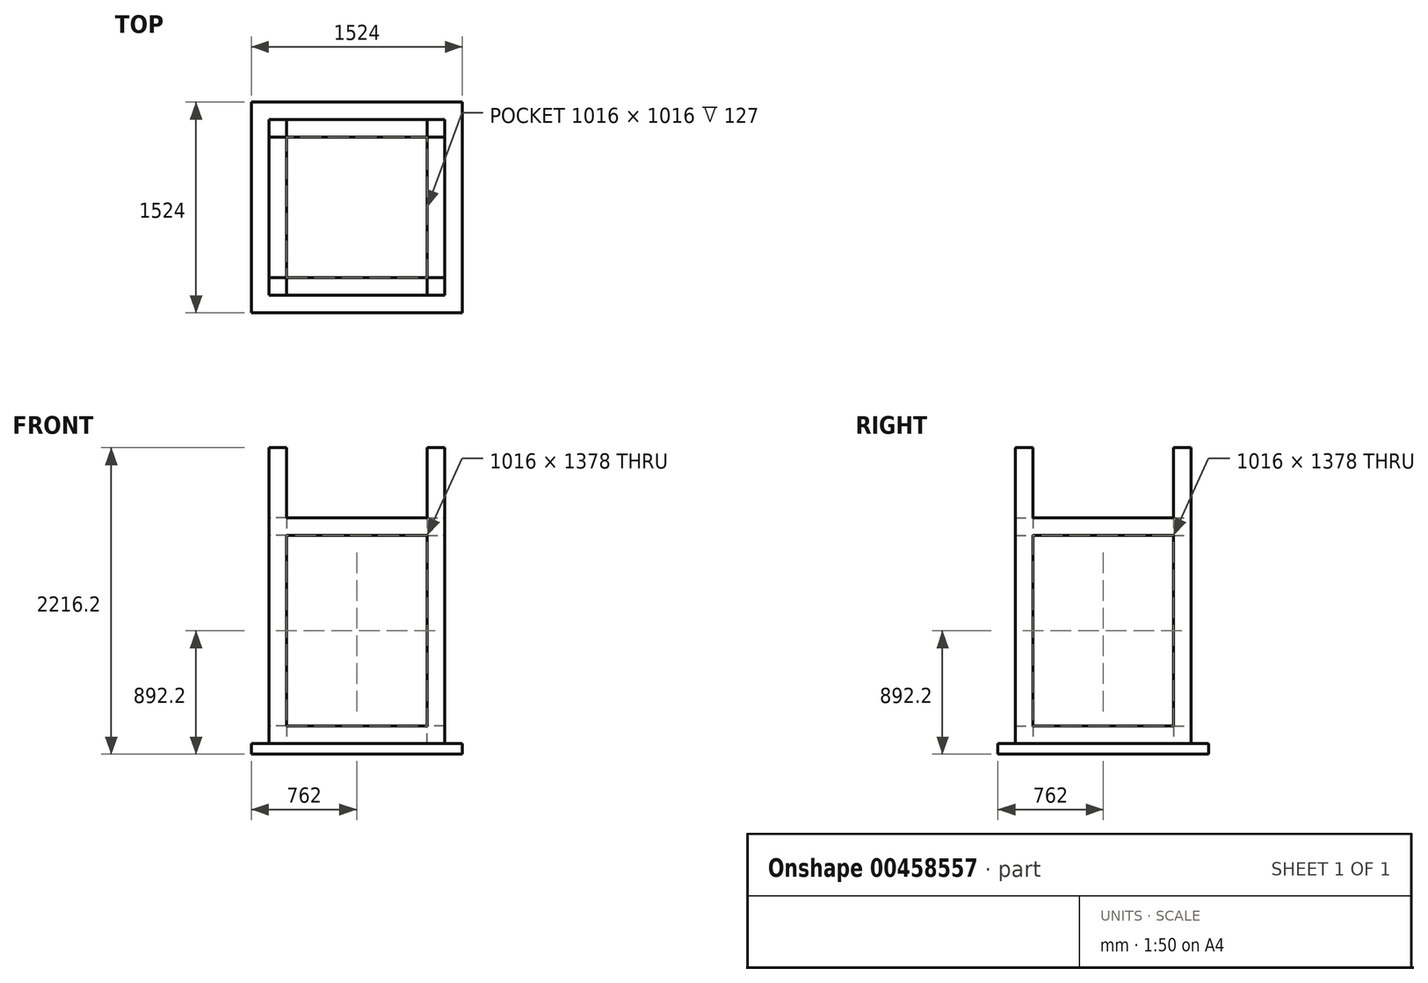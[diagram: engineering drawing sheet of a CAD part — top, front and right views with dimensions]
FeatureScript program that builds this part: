
annotation { "Feature Type Name" : "Feature", "Feature Type Description" : "" }
export const myFeature = defineFeature(function(context is Context, id is Id, definition is map)
    precondition{}
    {
        {
            var Q0;
            Q0=qCreatedBy(makeId("Top.planeOp"),FACE);
            var sketch = newSketch(context, id + "F0", { "sketchPlane" : qUnion([Q0])});
            skLineSegment(sketch, "E0.bottom", {"start": v(0, 1524) * mm, "end": v(1524, 1524) * mm});
            skLineSegment(sketch, "E0.top", {"start": v(0, 0) * mm, "end": v(1524, 0) * mm});
            skLineSegment(sketch, "E0.left", {"start": v(0, 1524) * mm, "end": v(0, 0) * mm});
            skLineSegment(sketch, "E0.right", {"start": v(1524, 1524) * mm, "end": v(1524, 0) * mm});
            skLineSegment(sketch, "E1.bottom", {"start": v(127, 1397) * mm, "end": v(254, 1397) * mm});
            skLineSegment(sketch, "E1.top", {"start": v(127, 1270) * mm, "end": v(254, 1270) * mm});
            skLineSegment(sketch, "E1.left", {"start": v(127, 1397) * mm, "end": v(127, 1270) * mm});
            skLineSegment(sketch, "E1.right", {"start": v(254, 1397) * mm, "end": v(254, 1270) * mm});
            skLineSegment(sketch, "E2.bottom", {"start": v(1270, 1397) * mm, "end": v(1397, 1397) * mm});
            skLineSegment(sketch, "E2.top", {"start": v(1270, 1270) * mm, "end": v(1397, 1270) * mm});
            skLineSegment(sketch, "E2.left", {"start": v(1270, 1397) * mm, "end": v(1270, 1270) * mm});
            skLineSegment(sketch, "E2.right", {"start": v(1397, 1397) * mm, "end": v(1397, 1270) * mm});
            skLineSegment(sketch, "E3.bottom", {"start": v(1270, 254) * mm, "end": v(1397, 254) * mm});
            skLineSegment(sketch, "E3.top", {"start": v(1270, 127) * mm, "end": v(1397, 127) * mm});
            skLineSegment(sketch, "E3.left", {"start": v(1270, 254) * mm, "end": v(1270, 127) * mm});
            skLineSegment(sketch, "E3.right", {"start": v(1397, 254) * mm, "end": v(1397, 127) * mm});
            skLineSegment(sketch, "E4.bottom", {"start": v(127, 254) * mm, "end": v(254, 254) * mm});
            skLineSegment(sketch, "E4.top", {"start": v(127, 127) * mm, "end": v(254, 127) * mm});
            skLineSegment(sketch, "E4.left", {"start": v(127, 254) * mm, "end": v(127, 127) * mm});
            skLineSegment(sketch, "E4.right", {"start": v(254, 254) * mm, "end": v(254, 127) * mm});
            skSolve(sketch);
        }
        {
            var Q0;
            Q0=makeQuery(id+"F0.imprint","IMPRINT",FACE,{"disambiguationData":[TD([[makeQuery(id+"F0.imprint","IMPRINT",EDGE,{"derivedFrom":sQuery(id+"F0.wireOp",EDGE,"E1.bottom")}),-1.0]])]});
            var Q1;
            Q1=makeQuery(id+"F0.imprint","IMPRINT",FACE,{"disambiguationData":[TD([[makeQuery(id+"F0.imprint","IMPRINT",EDGE,{"derivedFrom":sQuery(id+"F0.wireOp",EDGE,"E2.bottom")}),-1.0]])]});
            var Q2;
            Q2=makeQuery(id+"F0.imprint","IMPRINT",FACE,{"disambiguationData":[TD([[makeQuery(id+"F0.imprint","IMPRINT",EDGE,{"derivedFrom":sQuery(id+"F0.wireOp",EDGE,"E3.bottom")}),-1.0]])]});
            var Q3;
            Q3=makeQuery(id+"F0.imprint","IMPRINT",FACE,{"disambiguationData":[TD([[makeQuery(id+"F0.imprint","IMPRINT",EDGE,{"derivedFrom":sQuery(id+"F0.wireOp",EDGE,"E4.bottom")}),-1.0]])]});
            extrude(context, id + "F1", {"entities" : qUnion([Q0, Q1, Q2, Q3]), "depth" : 2140 * mm});
        }
        {
            var Q0;
            Q0=makeQuery(id+"F0.imprint","IMPRINT",FACE,{"disambiguationData":[TD([[makeQuery(id+"F0.imprint","IMPRINT",EDGE,{"derivedFrom":sQuery(id+"F0.wireOp",EDGE,"E0.bottom")}),-1.0]])]});
            var Q1;
            Q1=makeQuery(id+"F0.imprint","IMPRINT",FACE,{"disambiguationData":[TD([[makeQuery(id+"F0.imprint","IMPRINT",EDGE,{"derivedFrom":sQuery(id+"F0.wireOp",EDGE,"E1.bottom")}),-1.0]])]});
            var Q2;
            Q2=makeQuery(id+"F0.imprint","IMPRINT",FACE,{"disambiguationData":[TD([[makeQuery(id+"F0.imprint","IMPRINT",EDGE,{"derivedFrom":sQuery(id+"F0.wireOp",EDGE,"E2.bottom")}),-1.0]])]});
            var Q3;
            Q3=makeQuery(id+"F0.imprint","IMPRINT",FACE,{"disambiguationData":[TD([[makeQuery(id+"F0.imprint","IMPRINT",EDGE,{"derivedFrom":sQuery(id+"F0.wireOp",EDGE,"E3.bottom")}),-1.0]])]});
            var Q4;
            Q4=makeQuery(id+"F0.imprint","IMPRINT",FACE,{"disambiguationData":[TD([[makeQuery(id+"F0.imprint","IMPRINT",EDGE,{"derivedFrom":sQuery(id+"F0.wireOp",EDGE,"E4.bottom")}),-1.0]])]});
            extrude(context, id + "F2", {"entities" : qUnion([Q0, Q1, Q2, Q3, Q4]), "operationType" : NewBodyOperationType.ADD, "oppositeDirection" : true, "depth" : 76.2 * mm});
        }
        {
            var Q0;
            Q0=makeQuery(id+"F1.opExtrude","SWEPT_FACE",FACE,{"disambiguationData":[OSD([sQuery(id+"F0.wireOp",EDGE,"E3.left")])]});
            var sketch = newSketch(context, id + "F3", { "sketchPlane" : qUnion([Q0])});
            skLineSegment(sketch, "E5.bottom", {"start": v(-127, 1505) * mm, "end": v(-254, 1505) * mm});
            skLineSegment(sketch, "E5.top", {"start": v(-127, 1632) * mm, "end": v(-254, 1632) * mm});
            skLineSegment(sketch, "E5.left", {"start": v(-127, 1505) * mm, "end": v(-127, 1632) * mm});
            skLineSegment(sketch, "E5.right", {"start": v(-254, 1505) * mm, "end": v(-254, 1632) * mm});
            skSolve(sketch);
        }
        {
            var Q0;
            Q0=makeQuery(id+"F1.opExtrude","SWEPT_FACE",FACE,{"disambiguationData":[OSD([sQuery(id+"F0.wireOp",EDGE,"E2.top")])]});
            var sketch = newSketch(context, id + "F4", { "sketchPlane" : qUnion([Q0])});
            skLineSegment(sketch, "E6.bottom", {"start": v(1270, 1632) * mm, "end": v(1397, 1632) * mm});
            skLineSegment(sketch, "E6.top", {"start": v(1270, 1505) * mm, "end": v(1397, 1505) * mm});
            skLineSegment(sketch, "E6.left", {"start": v(1270, 1632) * mm, "end": v(1270, 1505) * mm});
            skLineSegment(sketch, "E6.right", {"start": v(1397, 1632) * mm, "end": v(1397, 1505) * mm});
            skSolve(sketch);
        }
        {
            var Q0;
            Q0=makeQuery(id+"F1.opExtrude","SWEPT_FACE",FACE,{"disambiguationData":[OSD([sQuery(id+"F0.wireOp",EDGE,"E1.right")])]});
            var sketch = newSketch(context, id + "F5", { "sketchPlane" : qUnion([Q0])});
            skLineSegment(sketch, "E7.bottom", {"start": v(1397, 1632) * mm, "end": v(1270, 1632) * mm});
            skLineSegment(sketch, "E7.top", {"start": v(1397, 1505) * mm, "end": v(1270, 1505) * mm});
            skLineSegment(sketch, "E7.left", {"start": v(1397, 1632) * mm, "end": v(1397, 1505) * mm});
            skLineSegment(sketch, "E7.right", {"start": v(1270, 1632) * mm, "end": v(1270, 1505) * mm});
            skSolve(sketch);
        }
        {
            var Q0;
            Q0=makeQuery(id+"F1.opExtrude","SWEPT_FACE",FACE,{"disambiguationData":[OSD([sQuery(id+"F0.wireOp",EDGE,"E4.bottom")])]});
            var sketch = newSketch(context, id + "F6", { "sketchPlane" : qUnion([Q0])});
            skLineSegment(sketch, "E8.bottom", {"start": v(-127, 1632) * mm, "end": v(-254, 1632) * mm});
            skLineSegment(sketch, "E8.top", {"start": v(-127, 1505) * mm, "end": v(-254, 1505) * mm});
            skLineSegment(sketch, "E8.left", {"start": v(-127, 1632) * mm, "end": v(-127, 1505) * mm});
            skLineSegment(sketch, "E8.right", {"start": v(-254, 1632) * mm, "end": v(-254, 1505) * mm});
            skSolve(sketch);
        }
        {
            var Q0;
            Q0 = qSketchRegion(id + "F6", true);
            extrude(context, id + "F7", {"entities" : qUnion([Q0]), "operationType" : NewBodyOperationType.ADD, "depth" : 1080 * mm});
        }
        {
            var Q0;
            Q0=makeQuery(id+"F5.imprint","IMPRINT",FACE,{"disambiguationData":[TD([[makeQuery(id+"F5.imprint","IMPRINT",EDGE,{"derivedFrom":sQuery(id+"F5.wireOp",EDGE,"E7.bottom")}),1.0]])]});
            extrude(context, id + "F8", {"entities" : qUnion([Q0]), "operationType" : NewBodyOperationType.ADD, "depth" : 1080 * mm});
        }
        {
            var Q0;
            Q0=makeQuery(id+"F4.imprint","IMPRINT",FACE,{"disambiguationData":[TD([[makeQuery(id+"F4.imprint","IMPRINT",EDGE,{"derivedFrom":sQuery(id+"F4.wireOp",EDGE,"E6.bottom")}),-1.0]])]});
            extrude(context, id + "F9", {"entities" : qUnion([Q0]), "operationType" : NewBodyOperationType.ADD, "depth" : 1090 * mm});
        }
        {
            var Q0;
            Q0=makeQuery(id+"F3.imprint","IMPRINT",FACE,{"disambiguationData":[TD([[makeQuery(id+"F3.imprint","IMPRINT",EDGE,{"derivedFrom":sQuery(id+"F3.wireOp",EDGE,"E5.bottom")}),-1.0]])]});
            extrude(context, id + "F10", {"entities" : qUnion([Q0]), "operationType" : NewBodyOperationType.ADD, "depth" : 1070 * mm});
        }
        {
            var Q0;
            {var subQ0=makeQuery(id+"F8.opExtrude","SWEPT_FACE",FACE,{"disambiguationData":[OSD([sQuery(id+"F5.wireOp",EDGE,"E7.right")])]});var subQ1=makeQuery(id+"F1.opExtrude","SWEPT_FACE",FACE,{"disambiguationData":[OSD([sQuery(id+"F0.wireOp",EDGE,"E2.top")])]});Q0=makeQuery(id+"F9.boolean.opBoolean","SPLIT",FACE,{"disambiguationData":[TD([makeQuery(id+"F2.opExtrude","CAP_FACE",FACE,{"disambiguationData":[OSD([sQuery(id+"F0.wireOp",EDGE,"E0.bottom"),sQuery(id+"F0.wireOp",EDGE,"E0.top"),sQuery(id+"F0.wireOp",EDGE,"E0.left"),sQuery(id+"F0.wireOp",EDGE,"E0.right")])],"isStart":true})])],"derivedFrom":makeQuery(id+"F8.boolean.opBoolean","MERGE",FACE,{"derivedFrom":[subQ1,subQ0]})});}
            var sketch = newSketch(context, id + "F11", { "sketchPlane" : qUnion([Q0])});
            skLineSegment(sketch, "E9.bottom", {"start": v(1397, 0) * mm, "end": v(1270, 0) * mm});
            skLineSegment(sketch, "E9.top", {"start": v(1397, 127) * mm, "end": v(1270, 127) * mm});
            skLineSegment(sketch, "E9.left", {"start": v(1397, 0) * mm, "end": v(1397, 127) * mm});
            skLineSegment(sketch, "E9.right", {"start": v(1270, 0) * mm, "end": v(1270, 127) * mm});
            skSolve(sketch);
        }
        {
            var Q0;
            {var subQ0=makeQuery(id+"F9.opExtrude","SWEPT_FACE",FACE,{"disambiguationData":[OSD([sQuery(id+"F4.wireOp",EDGE,"E6.left")])]});var subQ1=makeQuery(id+"F1.opExtrude","SWEPT_FACE",FACE,{"disambiguationData":[OSD([sQuery(id+"F0.wireOp",EDGE,"E3.left")])]});Q0=makeQuery(id+"F10.boolean.opBoolean","SPLIT",FACE,{"disambiguationData":[TD([makeQuery(id+"F2.opExtrude","CAP_FACE",FACE,{"disambiguationData":[OSD([sQuery(id+"F0.wireOp",EDGE,"E0.bottom"),sQuery(id+"F0.wireOp",EDGE,"E0.top"),sQuery(id+"F0.wireOp",EDGE,"E0.left"),sQuery(id+"F0.wireOp",EDGE,"E0.right")])],"isStart":true})])],"derivedFrom":makeQuery(id+"F9.boolean.opBoolean","MERGE",FACE,{"derivedFrom":[subQ1,subQ0]})});}
            var sketch = newSketch(context, id + "F12", { "sketchPlane" : qUnion([Q0])});
            skLineSegment(sketch, "E10.bottom", {"start": v(-127, 0) * mm, "end": v(-254, 0) * mm});
            skLineSegment(sketch, "E10.top", {"start": v(-127, 127) * mm, "end": v(-254, 127) * mm});
            skLineSegment(sketch, "E10.left", {"start": v(-127, 0) * mm, "end": v(-127, 127) * mm});
            skLineSegment(sketch, "E10.right", {"start": v(-254, 0) * mm, "end": v(-254, 127) * mm});
            skSolve(sketch);
        }
        {
            var Q0;
            Q0=makeQuery(id+"F7.boolean.opBoolean","SPLIT",FACE,{"disambiguationData":[TD([makeQuery(id+"F7.opExtrude","SWEPT_FACE",FACE,{"disambiguationData":[OSD([sQuery(id+"F6.wireOp",EDGE,"E8.top")])]})])],"derivedFrom":makeQuery(id+"F1.opExtrude","SWEPT_FACE",FACE,{"disambiguationData":[OSD([sQuery(id+"F0.wireOp",EDGE,"E4.bottom")])]})});
            var sketch = newSketch(context, id + "F13", { "sketchPlane" : qUnion([Q0])});
            skLineSegment(sketch, "E11.bottom", {"start": v(-127, 0) * mm, "end": v(-254, 0) * mm});
            skLineSegment(sketch, "E11.top", {"start": v(-127, 127) * mm, "end": v(-254, 127) * mm});
            skLineSegment(sketch, "E11.left", {"start": v(-127, 0) * mm, "end": v(-127, 127) * mm});
            skLineSegment(sketch, "E11.right", {"start": v(-254, 0) * mm, "end": v(-254, 127) * mm});
            skSolve(sketch);
        }
        {
            var Q0;
            {var subQ0=makeQuery(id+"F1.opExtrude","SWEPT_FACE",FACE,{"disambiguationData":[OSD([sQuery(id+"F0.wireOp",EDGE,"E4.right")])]});var subQ1=makeQuery(id+"F1.opExtrude","SWEPT_FACE",FACE,{"disambiguationData":[OSD([sQuery(id+"F0.wireOp",EDGE,"E1.right")])]});var subQ2=makeQuery(id+"F7.opExtrude","SWEPT_FACE",FACE,{"disambiguationData":[OSD([sQuery(id+"F6.wireOp",EDGE,"E8.right")])]});Q0=makeQuery(id+"F8.boolean.opBoolean","SPLIT",FACE,{"disambiguationData":[TD([makeQuery(id+"F1.opExtrude","SWEPT_FACE",FACE,{"disambiguationData":[OSD([sQuery(id+"F0.wireOp",EDGE,"E1.bottom")])]}),makeQuery(id+"F1.opExtrude","SWEPT_FACE",FACE,{"disambiguationData":[OSD([sQuery(id+"F0.wireOp",EDGE,"E1.top")])]}),subQ1,makeQuery(id+"F1.opExtrude","SWEPT_FACE",FACE,{"disambiguationData":[OSD([sQuery(id+"F0.wireOp",EDGE,"E2.bottom")])]}),makeQuery(id+"F1.opExtrude","SWEPT_FACE",FACE,{"disambiguationData":[OSD([sQuery(id+"F0.wireOp",EDGE,"E2.top")])]}),subQ0,makeQuery(id+"F2.opExtrude","CAP_FACE",FACE,{"disambiguationData":[OSD([sQuery(id+"F0.wireOp",EDGE,"E0.bottom"),sQuery(id+"F0.wireOp",EDGE,"E0.top"),sQuery(id+"F0.wireOp",EDGE,"E0.left"),sQuery(id+"F0.wireOp",EDGE,"E0.right")])],"isStart":true}),makeQuery(id+"F7.opExtrude","SWEPT_FACE",FACE,{"disambiguationData":[OSD([sQuery(id+"F6.wireOp",EDGE,"E8.top")])]}),subQ2,makeQuery(id+"F8.opExtrude","SWEPT_FACE",FACE,{"disambiguationData":[OSD([sQuery(id+"F5.wireOp",EDGE,"E7.top")])]}),makeQuery(id+"F8.opExtrude","SWEPT_FACE",FACE,{"disambiguationData":[OSD([sQuery(id+"F5.wireOp",EDGE,"E7.left")])]}),makeQuery(id+"F8.opExtrude","SWEPT_FACE",FACE,{"disambiguationData":[OSD([sQuery(id+"F5.wireOp",EDGE,"E7.right")])]})])],"derivedFrom":makeQuery(id+"F7.boolean.opBoolean","MERGE",FACE,{"derivedFrom":[subQ1,subQ0,subQ2]})});}
            var sketch = newSketch(context, id + "F14", { "sketchPlane" : qUnion([Q0])});
            skLineSegment(sketch, "E12.bottom", {"start": v(1397, 0) * mm, "end": v(1270, 0) * mm});
            skLineSegment(sketch, "E12.top", {"start": v(1397, 127) * mm, "end": v(1270, 127) * mm});
            skLineSegment(sketch, "E12.left", {"start": v(1397, 0) * mm, "end": v(1397, 127) * mm});
            skLineSegment(sketch, "E12.right", {"start": v(1270, 0) * mm, "end": v(1270, 127) * mm});
            skSolve(sketch);
        }
        {
            var Q0;
            Q0=makeQuery(id+"F11.imprint","IMPRINT",FACE,{"disambiguationData":[TD([[makeQuery(id+"F11.imprint","IMPRINT",EDGE,{"derivedFrom":sQuery(id+"F11.wireOp",EDGE,"E9.bottom")}),1.0]])]});
            extrude(context, id + "F15", {"entities" : qUnion([Q0]), "operationType" : NewBodyOperationType.ADD, "depth" : 1060 * mm});
        }
        {
            var Q0;
            Q0=makeQuery(id+"F12.imprint","IMPRINT",FACE,{"disambiguationData":[TD([[makeQuery(id+"F12.imprint","IMPRINT",EDGE,{"derivedFrom":sQuery(id+"F12.wireOp",EDGE,"E10.bottom")}),1.0]])]});
            extrude(context, id + "F16", {"entities" : qUnion([Q0]), "operationType" : NewBodyOperationType.ADD, "depth" : 1090 * mm});
        }
        {
            var Q0;
            Q0=makeQuery(id+"F13.imprint","IMPRINT",FACE,{"disambiguationData":[TD([[makeQuery(id+"F13.imprint","IMPRINT",EDGE,{"derivedFrom":sQuery(id+"F13.wireOp",EDGE,"E11.bottom")}),-1.0]])]});
            extrude(context, id + "F17", {"entities" : qUnion([Q0]), "operationType" : NewBodyOperationType.ADD, "depth" : 1070 * mm});
        }
        {
            var Q0;
            Q0=makeQuery(id+"F14.imprint","IMPRINT",FACE,{"disambiguationData":[TD([[makeQuery(id+"F14.imprint","IMPRINT",EDGE,{"derivedFrom":sQuery(id+"F14.wireOp",EDGE,"E12.bottom")}),-1.0]])]});
            extrude(context, id + "F18", {"entities" : qUnion([Q0]), "operationType" : NewBodyOperationType.ADD, "depth" : 1100 * mm});
        }
    });
